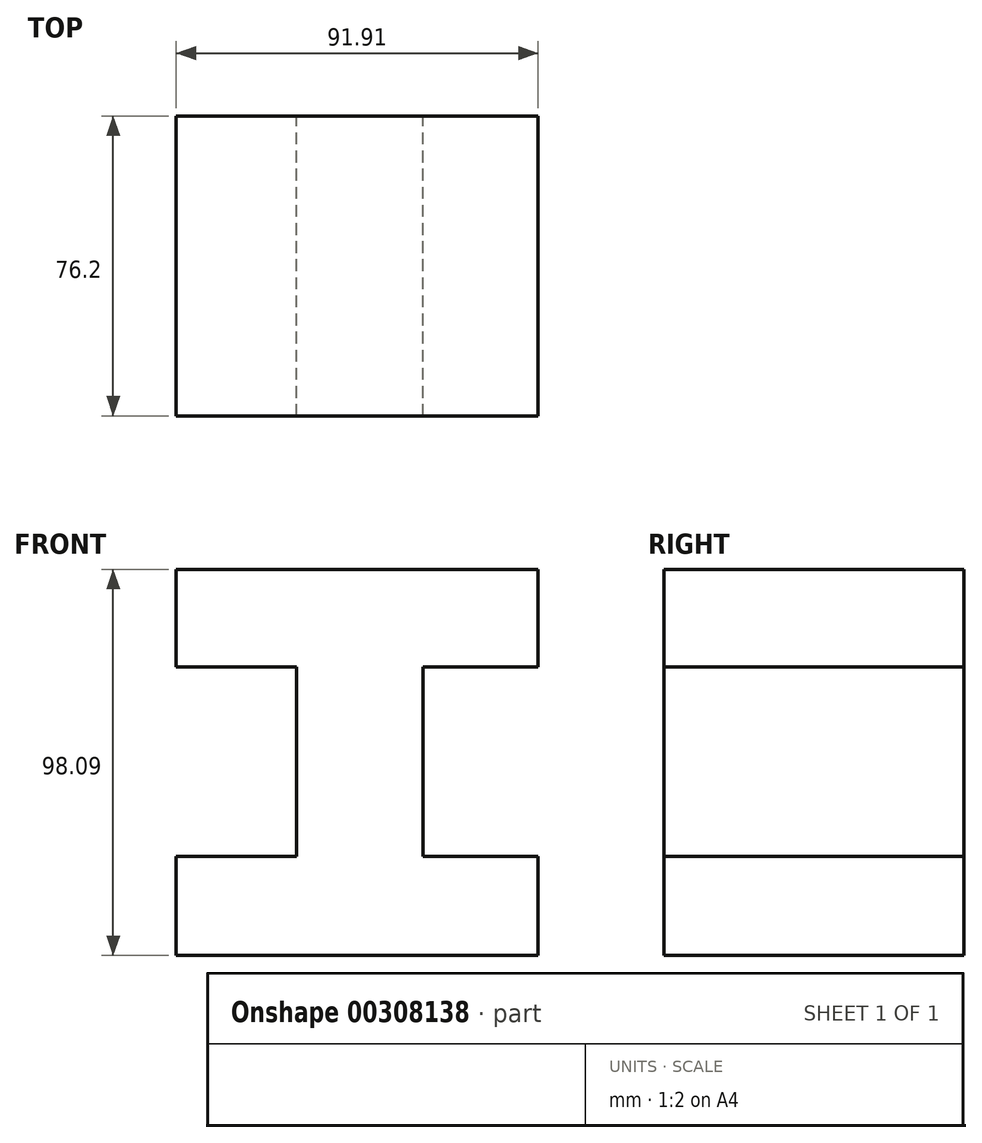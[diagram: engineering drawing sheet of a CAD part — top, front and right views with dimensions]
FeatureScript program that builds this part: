
annotation { "Feature Type Name" : "Feature", "Feature Type Description" : "" }
export const myFeature = defineFeature(function(context is Context, id is Id, definition is map)
    precondition{}
    {
        {
            var Q0;
            Q0=qCreatedBy(makeId("Front.planeOp"),FACE);
            var sketch = newSketch(context, id + "F0", { "sketchPlane" : qUnion([Q0])});
            skLineSegment(sketch, "E0", {"start": v(-41.98, -37.78) * mm, "end": v(49.93, -37.78) * mm});
            skLineSegment(sketch, "E1", {"start": v(49.93, -37.78) * mm, "end": v(49.93, -12.6) * mm});
            skLineSegment(sketch, "E2", {"start": v(49.93, -12.6) * mm, "end": v(20.77, -12.6) * mm});
            skLineSegment(sketch, "E3", {"start": v(20.77, -12.6) * mm, "end": v(20.77, 35.57) * mm});
            skLineSegment(sketch, "E4", {"start": v(20.77, 35.57) * mm, "end": v(49.93, 35.57) * mm});
            skLineSegment(sketch, "E5", {"start": v(49.93, 35.57) * mm, "end": v(49.93, 60.31) * mm});
            skLineSegment(sketch, "E6", {"start": v(49.93, 60.31) * mm, "end": v(-41.98, 60.31) * mm});
            skLineSegment(sketch, "E7", {"start": v(-41.98, 60.31) * mm, "end": v(-41.98, 35.57) * mm});
            skLineSegment(sketch, "E8", {"start": v(-41.98, 35.57) * mm, "end": v(-11.49, 35.57) * mm});
            skLineSegment(sketch, "E9", {"start": v(-11.49, 35.57) * mm, "end": v(-11.49, -12.6) * mm});
            skLineSegment(sketch, "E10", {"start": v(-11.49, -12.6) * mm, "end": v(-41.98, -12.6) * mm});
            skLineSegment(sketch, "E11", {"start": v(-41.98, -12.6) * mm, "end": v(-41.98, -37.78) * mm});
            skSolve(sketch);
        }
        {
            var Q0;
            Q0=makeQuery(id+"F0.imprint","IMPRINT",FACE,{"disambiguationData":[TD([[makeQuery(id+"F0.imprint","IMPRINT",EDGE,{"derivedFrom":sQuery(id+"F0.wireOp",EDGE,"E0")}),1.0]])]});
            extrude(context, id + "F1", {"entities" : qUnion([Q0]), "depth" : 76.2 * mm});
        }
    });
